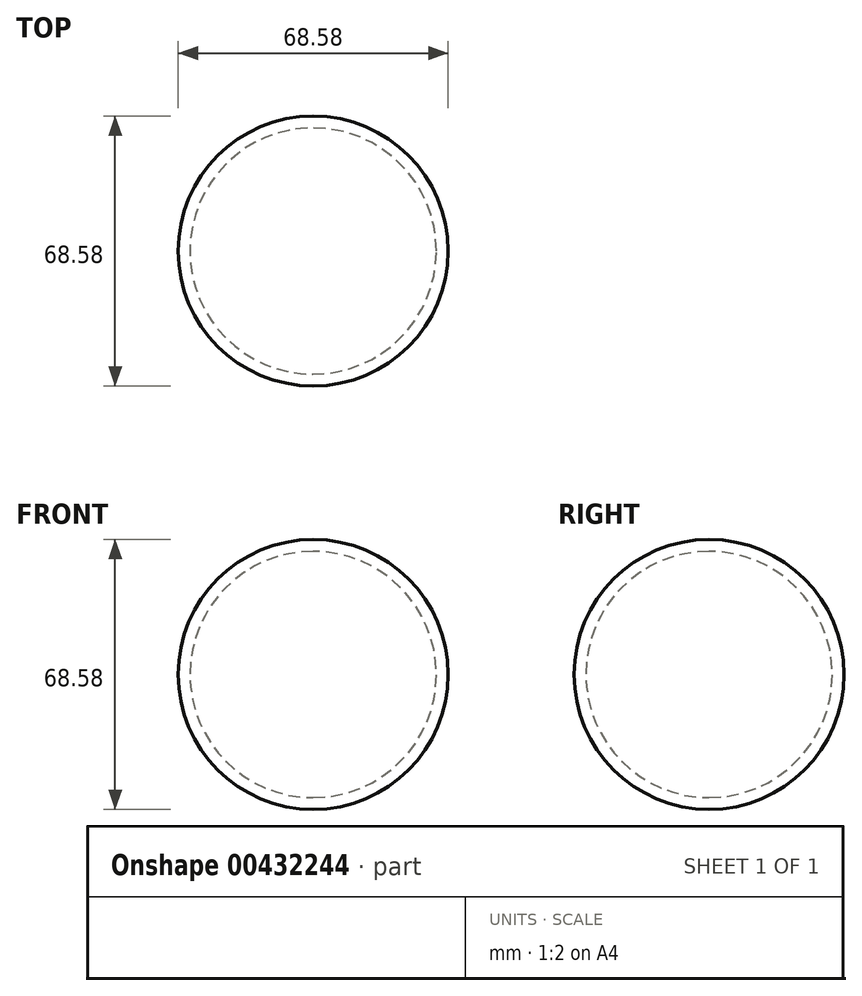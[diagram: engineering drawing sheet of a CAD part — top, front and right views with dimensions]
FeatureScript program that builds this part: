
annotation { "Feature Type Name" : "Feature", "Feature Type Description" : "" }
export const myFeature = defineFeature(function(context is Context, id is Id, definition is map)
    precondition{}
    {
        {
            var Q0;
            Q0=qCreatedBy(makeId("Front.planeOp"),FACE);
            var sketch = newSketch(context, id + "F0", { "sketchPlane" : qUnion([Q0])});
            skLineSegment(sketch, "E0", {"start": v(0, 0) * mm, "end": v(0, 68.58) * mm});
            skPoint(sketch, "E1.center.orphan", {"position": v(0, 34.3) * mm});
            skArc(sketch, "E2", {"start": v(0, 68.58) * mm, "mid": v(34.3, 34.3) * mm, "end": v(0, 0) * mm});
            skSolve(sketch);
        }
        {
            var Q0;
            Q0=makeQuery(id+"F0.imprint","IMPRINT",FACE,{"disambiguationData":[TD([[makeQuery(id+"F0.imprint","IMPRINT",EDGE,{"derivedFrom":sQuery(id+"F0.wireOp",EDGE,"E0")}),-1.0]])]});
            var Q1;
            Q1=sQuery(id+"F0.wireOp",EDGE,"E0");
            revolve(context, id + "F1", {"entities" : qUnion([Q0]), "axis" : qUnion([Q1]), "revolveType" : RevolveType.FULL});
        }
        {
            var Q0;
            Q0=makeQuery(id+"F1.opRevolve","SWEPT_FACE",FACE,{"disambiguationData":[OSD([sQuery(id+"F0.wireOp",EDGE,"E2")])]});
            var Q1;
            Q1=makeQuery(id+"F1.opRevolve","SWEPT_BODY",BODY,{"disambiguationData":[OSD([sQuery(id+"F0.wireOp",EDGE,"E0"),sQuery(id+"F0.wireOp",EDGE,"E2")])]});
            shell(context, id + "F2", {"isHollow" : true, "entities" : qUnion([Q0]), "parts" : qUnion([Q1]), "thickness" : 3 * mm});
        }
        {
            var Q0;
            Q0=qCreatedBy(makeId("Top.planeOp"),FACE);
            cPlane(context, id + "F3", {"entities" : qUnion([Q0]), "cplaneType" : CPlaneType.OFFSET, "offset" : 34.3 * mm, "width" : 152.4 * mm, "height" : 152.4 * mm});
        }
    });
